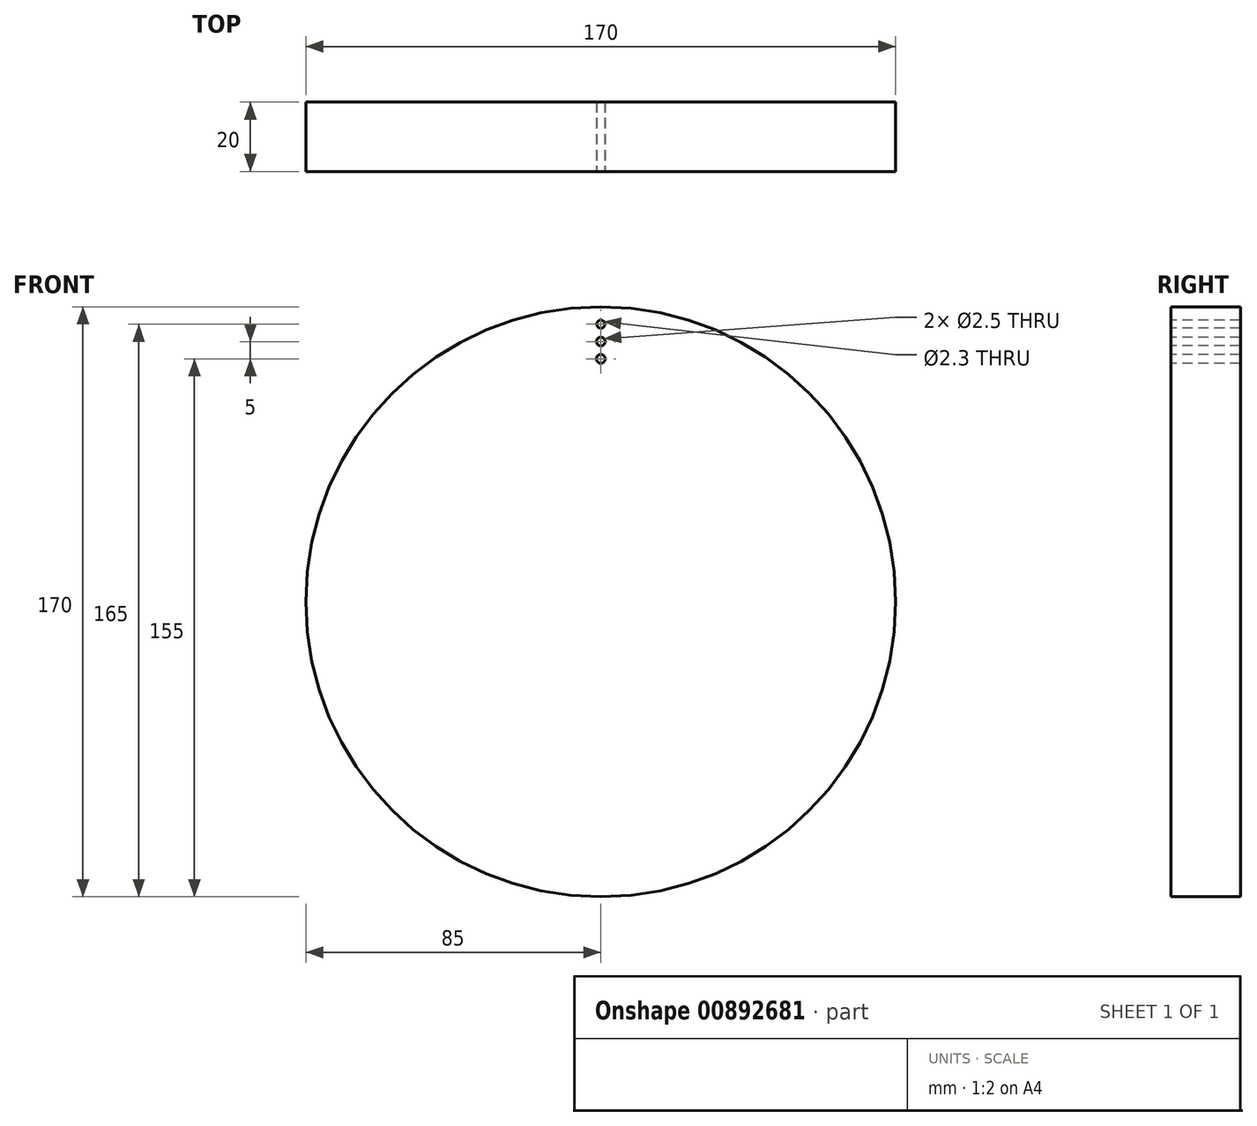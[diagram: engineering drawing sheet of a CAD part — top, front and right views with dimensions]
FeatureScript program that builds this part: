
annotation { "Feature Type Name" : "Feature", "Feature Type Description" : "" }
export const myFeature = defineFeature(function(context is Context, id is Id, definition is map)
    precondition{}
    {
        {
            var Q0;
            Q0=qCreatedBy(makeId("Front.planeOp"),FACE);
            var sketch = newSketch(context, id + "F0", { "sketchPlane" : qUnion([Q0])});
            skCircle(sketch, "E0", {"center": v(0, 0) * mm, "radius": 85 * mm});
            skSolve(sketch);
        }
        {
            var Q0;
            Q0=qSketchRegion(id+"F0",true);
            var Q1;
            Q1=sQuery(id+"F0.wireOp",EDGE,"E0");
            extrude(context, id + "F1", {"entities" : qUnion([Q0]), "surfaceEntities" : qUnion([Q1]), "depth" : 20 * mm, "offsetDistance" : 25 * mm});
        }
        {
            var Q0;
            Q0=makeQuery(id+"F1.opExtrude","CAP_FACE",FACE,{"disambiguationData":[OSD([sQuery(id+"F0.wireOp",EDGE,"E0")])],"isStart":false});
            var sketch = newSketch(context, id + "F2", { "sketchPlane" : qUnion([Q0])});
            skCircle(sketch, "E1", {"center": v(0, 75) * mm, "radius": 1.25 * mm});
            skCircle(sketch, "E2", {"center": v(0, 70) * mm, "radius": 1.25 * mm});
            skCircle(sketch, "E3", {"center": v(0, 80) * mm, "radius": 1.15 * mm});
            skSolve(sketch);
        }
        {
            var Q0;
            Q0=qSketchRegion(id+"F2",true);
            extrude(context, id + "F3", {"entities" : qUnion([Q0]), "operationType" : NewBodyOperationType.REMOVE, "oppositeDirection" : true, "depth" : 25 * mm, "offsetDistance" : 25 * mm});
        }
    });
